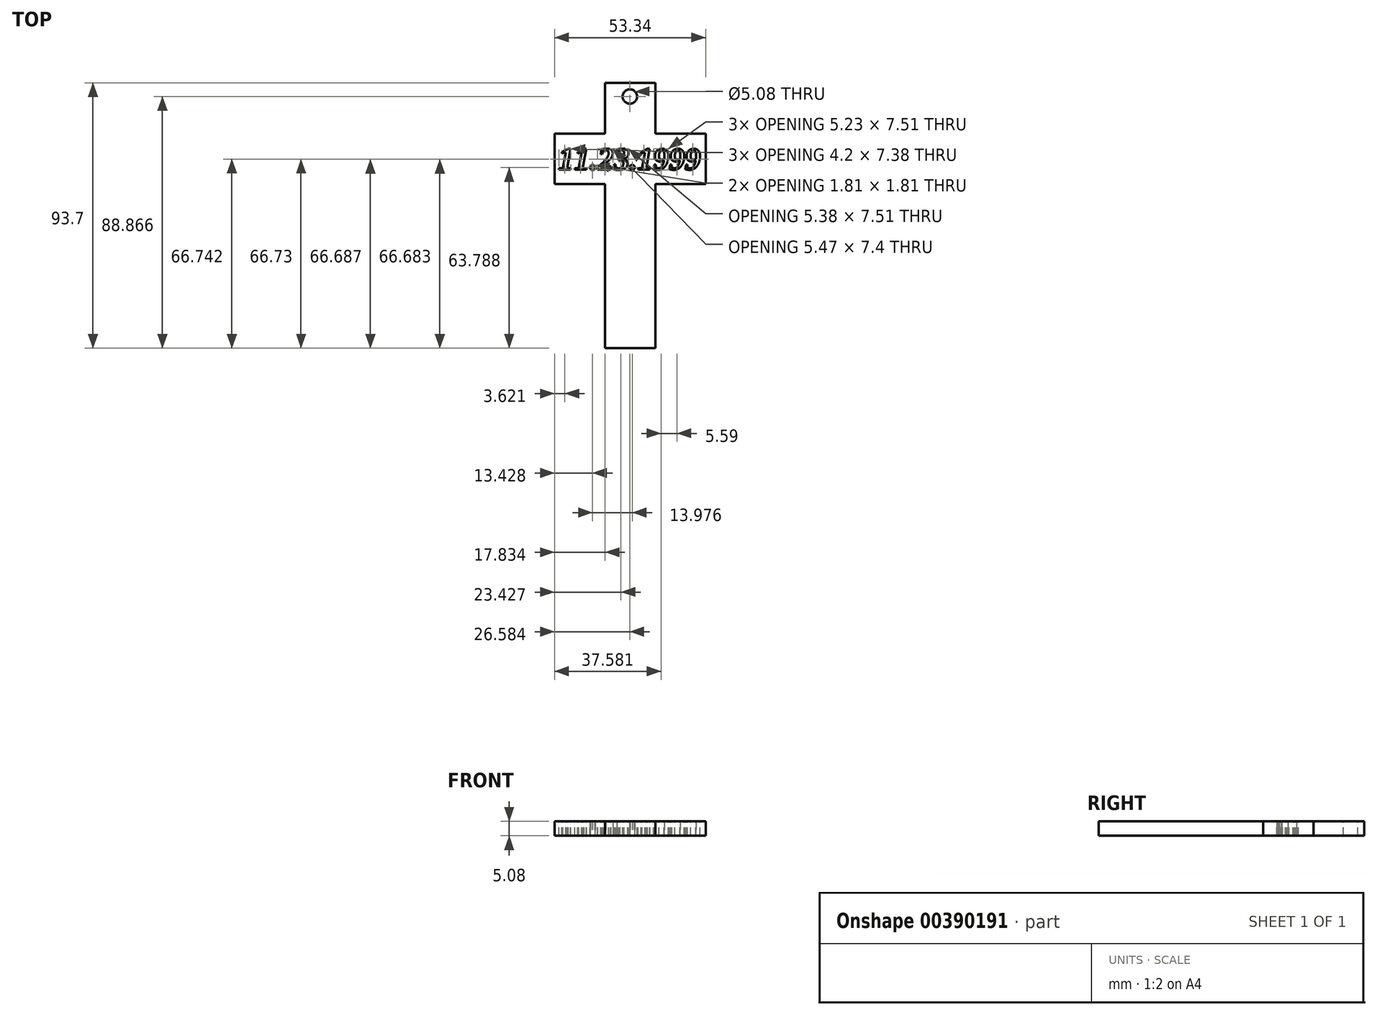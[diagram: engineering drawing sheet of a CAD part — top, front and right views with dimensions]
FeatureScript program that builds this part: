
annotation { "Feature Type Name" : "Feature", "Feature Type Description" : "" }
export const myFeature = defineFeature(function(context is Context, id is Id, definition is map)
    precondition{}
    {
        {
            var Q0;
            Q0=qCreatedBy(makeId("Top.planeOp"),FACE);
            var sketch = newSketch(context, id + "F0", { "sketchPlane" : qUnion([Q0])});
            skLineSegment(sketch, "E0.bottom", {"start": v(-18.47, 41.08) * mm, "end": v(-0.69, 41.08) * mm});
            skLineSegment(sketch, "E0.top", {"start": v(-18.47, -52.62) * mm, "end": v(-0.69, -52.62) * mm});
            skLineSegment(sketch, "E0.left", {"start": v(-18.47, 41.08) * mm, "end": v(-18.47, 23.15) * mm});
            skLineSegment(sketch, "E0.right", {"start": v(-0.69, 41.08) * mm, "end": v(-0.69, 23.15) * mm});
            skLineSegment(sketch, "E1.bottom", {"start": v(-36.25, 23.15) * mm, "end": v(-18.47, 23.15) * mm});
            skLineSegment(sketch, "E1.top", {"start": v(-36.25, 5.37) * mm, "end": v(-18.47, 5.37) * mm});
            skLineSegment(sketch, "E1.left", {"start": v(-36.25, 23.15) * mm, "end": v(-36.25, 5.37) * mm});
            skLineSegment(sketch, "E1.right", {"start": v(17.1, 23.15) * mm, "end": v(17.1, 5.37) * mm});
            skLineSegment(sketch, "E2", {"start": v(-18.47, 23.15) * mm, "end": v(-18.47, 41.08) * mm});
            skLineSegment(sketch, "E3", {"start": v(17.1, 23.15) * mm, "end": v(-0.69, 23.15) * mm});
            skLineSegment(sketch, "E4", {"start": v(-18.47, 5.37) * mm, "end": v(-18.47, -52.62) * mm});
            skLineSegment(sketch, "E5", {"start": v(-0.69, 23.15) * mm, "end": v(17.1, 23.15) * mm});
            skLineSegment(sketch, "E6", {"start": v(-0.69, 5.37) * mm, "end": v(-0.69, -52.62) * mm});
            skLineSegment(sketch, "E7", {"start": v(-0.69, 5.37) * mm, "end": v(17.1, 5.37) * mm});
            skSolve(sketch);
        }
        {
            var Q0;
            Q0=makeQuery(id+"F0.imprint","IMPRINT",FACE,{"disambiguationData":[TD([[makeQuery(id+"F0.imprint","IMPRINT",EDGE,{"derivedFrom":sQuery(id+"F0.wireOp",EDGE,"E0.bottom")}),-1.0]])]});
            extrude(context, id + "F1", {"entities" : qUnion([Q0]), "depth" : 5.08 * mm});
        }
        {
            var Q0;
            Q0=makeQuery(id+"F1.opExtrude","CAP_FACE",FACE,{"disambiguationData":[OSD([sQuery(id+"F0.wireOp",EDGE,"E0.bottom"),sQuery(id+"F0.wireOp",EDGE,"E0.top"),sQuery(id+"F0.wireOp",EDGE,"E0.right"),sQuery(id+"F0.wireOp",EDGE,"E1.top"),sQuery(id+"F0.wireOp",EDGE,"E1.left"),sQuery(id+"F0.wireOp",EDGE,"E1.right"),sQuery(id+"F0.wireOp",EDGE,"E1.bottom"),sQuery(id+"F0.wireOp",EDGE,"E2"),sQuery(id+"F0.wireOp",EDGE,"E4"),sQuery(id+"F0.wireOp",EDGE,"E5"),sQuery(id+"F0.wireOp",EDGE,"E6"),sQuery(id+"F0.wireOp",EDGE,"E7")])],"isStart":false});
            var sketch = newSketch(context, id + "F2", { "sketchPlane" : qUnion([Q0])});
            skText(sketch, "E8", { "text": "11.23.1999", "fontName": "Tinos-BoldItalic.ttf"});
            const initialGuessF2  = {"E8": [-0.03499, 0.01042, 1, 0, 0.00805]};
            skSetInitialGuess(sketch, initialGuessF2);
            skSolve(sketch);
        }
        {
            var Q0;
            Q0 = qSketchRegion(id + "F2", true);
            extrude(context, id + "F3", {"entities" : qUnion([Q0]), "operationType" : NewBodyOperationType.REMOVE, "oppositeDirection" : true, "depth" : 25.4 * mm});
        }
        {
            var Q0;
            {var subQ0=sQuery(id+"F0.wireOp",EDGE,"E7");var subQ1=sQuery(id+"F0.wireOp",EDGE,"E6");var subQ2=sQuery(id+"F0.wireOp",EDGE,"E0.right");var subQ3=sQuery(id+"F0.wireOp",EDGE,"E0.top");var subQ4=sQuery(id+"F0.wireOp",EDGE,"E1.top");var subQ5=sQuery(id+"F0.wireOp",EDGE,"E0.bottom");var subQ6=sQuery(id+"F0.wireOp",EDGE,"E5");var subQ7=sQuery(id+"F0.wireOp",EDGE,"E1.left");var subQ8=sQuery(id+"F0.wireOp",EDGE,"E1.right");var subQ9=sQuery(id+"F0.wireOp",EDGE,"E1.bottom");var subQ10=sQuery(id+"F0.wireOp",EDGE,"E2");var subQ11=sQuery(id+"F0.wireOp",EDGE,"E4");Q0=makeQuery(id+"F3.boolean.opBoolean","SPLIT",FACE,{"disambiguationData":[TD([makeQuery(id+"F1.opExtrude","SWEPT_FACE",FACE,{"disambiguationData":[OSD([subQ5])]})])],"derivedFrom":makeQuery(id+"F1.opExtrude","CAP_FACE",FACE,{"disambiguationData":[OSD([subQ5,subQ3,subQ2,subQ4,subQ7,subQ8,subQ9,subQ10,subQ11,subQ6,subQ1,subQ0])],"isStart":false})});}
            var sketch = newSketch(context, id + "F4", { "sketchPlane" : qUnion([Q0])});
            skCircle(sketch, "E9", {"center": v(-9.67, 36.25) * mm, "radius": 2.54 * mm});
            skSolve(sketch);
        }
        {
            var Q0;
            Q0=makeQuery(id+"F4.imprint","IMPRINT",FACE,{"disambiguationData":[TD([[makeQuery(id+"F4.imprint","IMPRINT",EDGE,{"derivedFrom":sQuery(id+"F4.wireOp",EDGE,"E9")}),1.0]])]});
            extrude(context, id + "F5", {"entities" : qUnion([Q0]), "operationType" : NewBodyOperationType.REMOVE, "oppositeDirection" : true, "depth" : 25.4 * mm});
        }
    });
